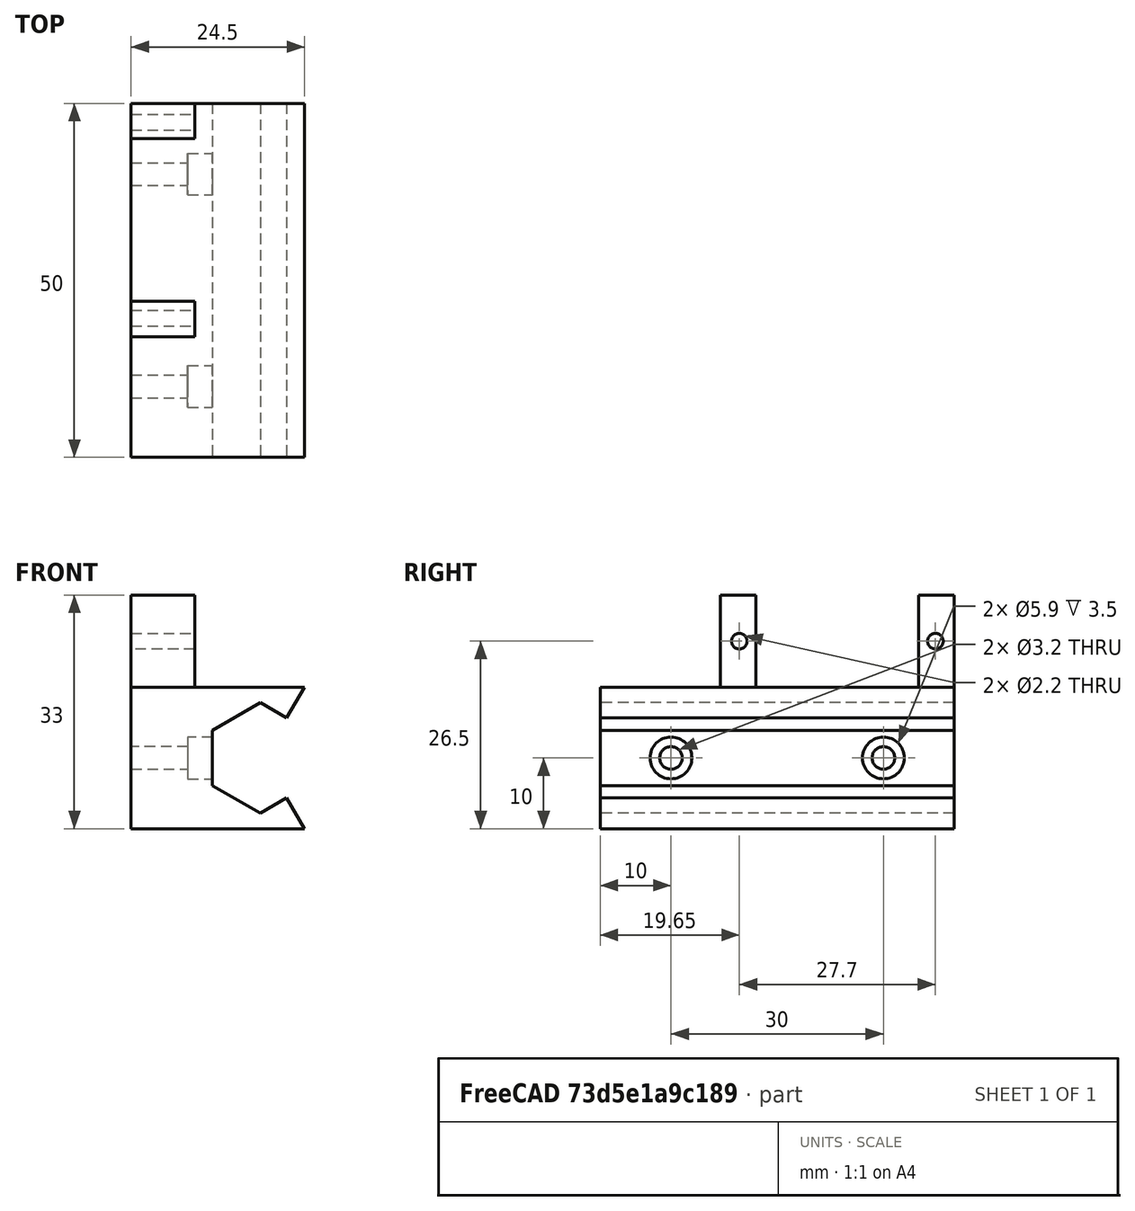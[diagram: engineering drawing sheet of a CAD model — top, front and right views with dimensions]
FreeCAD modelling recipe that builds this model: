
FCSTD DOCUMENT  (FreeCAD 1.0R39109 (Git))
Label: buzzMeIN
License: All rights reserved
LicenseURL: https://en.wikipedia.org/wiki/All_rights_reserved
objects: Sketcher::SketchObject×3, PartDesign::Body×2, PartDesign::Pad×2, PartDesign::SubShapeBinder×2, PartDesign::Pocket×2, Mesh::Feature×1
note: 22 computed .brp shape members not serialized (recipe doc carries the construction recipe); baked Part::Feature solids carry a one-line shape summary decoded from their .brp

FEATURE [PartDesign::Body] Body  label="Körper"
  AllowCompound = false
  Origin = -> Origin
FEATURE [Mesh::Feature] buzzMeIn_Penmover  label="buzzMeIn-Penmover"
FEATURE [Sketcher::SketchObject] Sketch
  ArcFitTolerance = 1e-06
  AttachmentSupport = -> [XZ_Plane001]
  FullyConstrained = true
  MakeInternals = false
  MapMode = 5
  Placement = pos=(0,0,0) rot=(1,0,0;1.5708rad)
  sketch-geometry (15):
    g0: LineSegment StartX=0 StartY=7.8 StartZ=0 EndX=-6.755 EndY=3.9 EndZ=0
    g1: LineSegment StartX=-6.755 StartY=3.9 StartZ=0 EndX=-6.755 EndY=-3.9 EndZ=0
    g2: LineSegment StartX=-6.755 StartY=-3.9 StartZ=0 EndX=0 EndY=-7.8 EndZ=0
    g3: Circle [constr] CenterX=0 CenterY=0 CenterZ=0 NormalX=0 NormalY=0 NormalZ=1 AngleXU=0 Radius=7.8
    g4: LineSegment StartX=3.72391 StartY=5.65 StartZ=0 EndX=0 EndY=7.8 EndZ=0
    g5: LineSegment StartX=0 StartY=-7.8 StartZ=0 EndX=3.72391 EndY=-5.65 EndZ=0
    g6: LineSegment [constr] StartX=3.72391 StartY=5.65 StartZ=0 EndX=3.72391 EndY=-5.65 EndZ=0
    g7: LineSegment [constr] StartX=3.72391 StartY=-5.65 StartZ=0 EndX=6.755 EndY=-3.9 EndZ=0
    g8: LineSegment [constr] StartX=3.72391 StartY=5.65 StartZ=0 EndX=6.755 EndY=3.9 EndZ=0
    g9: LineSegment [constr] StartX=6.755 StartY=3.9 StartZ=0 EndX=6.755 EndY=-3.9 EndZ=0
    g10: LineSegment StartX=3.72391 StartY=-5.65 StartZ=0 EndX=6.23538 EndY=-10 EndZ=0
    g11: LineSegment StartX=6.23538 StartY=-10 StartZ=0 EndX=-9.26 EndY=-10 EndZ=0
    g12: LineSegment StartX=-9.26 StartY=-10 StartZ=0 EndX=-9.26 EndY=10 EndZ=0
    g13: LineSegment StartX=-9.26 StartY=10 StartZ=0 EndX=6.23538 EndY=10 EndZ=0
    g14: LineSegment StartX=3.72391 StartY=5.65 StartZ=0 EndX=6.23538 EndY=10 EndZ=0
  constraints (41):
    c: Coincident(g0,g1)
    c: Coincident(g1,g2)
    c: Coincident(g2,g5)
    c: Coincident(g4,g0)
    c: Equal(g0,g1)
    c: Equal(g0,g2)
    c: PointOnObject(g0,g3)
    c: PointOnObject(g1,g3)
    c: PointOnObject(g2,g3)
    c: PointOnObject(g4,g3)
    c: Coincident(g3,g-1)
    c: PointOnObject(g0,g-2)
    c: Diameter(g3) = 15.6
    c: Vertical(g6)
    c: PointOnObject(g7,g3)
    c: PointOnObject(g8,g3)
    c: Parallel(g8,g4)
    c: Parallel(g7,g5)
    c: Coincident(g9,g8)
    c: Coincident(g9,g7)
    c: Vertical(g9)
    c: Equal(g9,g0)
    c: PointOnObject(g2,g-2)
    c: Horizontal(g11)
    c: Coincident(g12,g11)
    c: Vertical(g12)
    c: Coincident(g13,g12)
    c: Horizontal(g13)
    c: DistanceY(g12,g12) = 20
    c: Distance(g12,g-2) = 9.26
    c: Symmetric(g10,g13,g-1)
    c: Coincident(g5,g10)
    c: Coincident(g5,g7)
    c: Coincident(g4,g14)
    c: Coincident(g4,g8)
    c: Coincident(g6,g4)
    c: Coincident(g14,g13)
    c: Coincident(g6,g5)
    c: Coincident(g10,g11)
    c: Distance(g5,g5) = 4.3
    c: Angle(g10,g11) = 1.0472
FEATURE [PartDesign::Pad] Pad
  Direction = (0,-1,2e-16)
  Length = 50
  Length2 = 10
  Placement = pos=(0,0,0) rot=(1,0,0;1.5708rad)
  Profile = -> Sketch
  ReferenceAxis = -> Sketch [N_Axis]
  Refine = true
  Suppressed = false
  Type = 0
FEATURE [Sketcher::SketchObject] Sketch001
  ArcFitTolerance = 1e-06
  AttachmentSupport = -> [Pad]
  ExternalGeometry = -> [Pad]
  FullyConstrained = true
  MakeInternals = false
  MapMode = 5
  Placement = pos=(-9.26,0,0) rot=(0.707107,0,-0.707107;3.14159rad)
  sketch-geometry (15):
    g0: LineSegment StartX=-10 StartY=-2.7e-15 StartZ=0 EndX=10 EndY=-2.7e-15 EndZ=0
    g1: LineSegment StartX=10 StartY=-2.7e-15 StartZ=0 EndX=10 EndY=50 EndZ=0
    g2: LineSegment StartX=-10 StartY=5 StartZ=0 EndX=-23 EndY=5 EndZ=0
    g3: LineSegment StartX=-23 StartY=5 StartZ=0 EndX=-23 EndY=-2.7e-15 EndZ=0
    g4: LineSegment StartX=-23 StartY=-2.7e-15 StartZ=0 EndX=-10 EndY=-2.7e-15 EndZ=0
    g5: LineSegment StartX=-10 StartY=33 StartZ=0 EndX=-23 EndY=33 EndZ=0
    g6: LineSegment StartX=-23 StartY=33 StartZ=0 EndX=-23 EndY=28 EndZ=0
    g7: LineSegment StartX=-23 StartY=28 StartZ=0 EndX=-10 EndY=28 EndZ=0
    g8: LineSegment StartX=-10 StartY=5 StartZ=0 EndX=-10 EndY=28 EndZ=0
    g9: Circle CenterX=-16.5 CenterY=30.35 CenterZ=0 NormalX=0 NormalY=0 NormalZ=1 AngleXU=0 Radius=1.1
    g10: Circle CenterX=-16.5 CenterY=2.65 CenterZ=0 NormalX=0 NormalY=0 NormalZ=1 AngleXU=0 Radius=1.1
    g11: LineSegment [constr] StartX=-16.5 StartY=30.35 StartZ=0 EndX=-16.5 EndY=2.65 EndZ=0
    g12: LineSegment [constr] StartX=-10 StartY=16.5 StartZ=0 EndX=-23 EndY=16.5 EndZ=0
    g13: LineSegment StartX=10 StartY=50 StartZ=0 EndX=-10 EndY=50 EndZ=0
    g14: LineSegment StartX=-10 StartY=50 StartZ=0 EndX=-10 EndY=33 EndZ=0
  constraints (38):
    c: Coincident(g0,g1)
    c: Coincident(g2,g3)
    c: Coincident(g3,g4)
    c: Vertical(g3)
    c: Horizontal(g2)
    c: Horizontal(g4)
    c: Coincident(g5,g6)
    c: Coincident(g6,g7)
    c: Horizontal(g5)
    c: Horizontal(g7)
    c: Vertical(g6)
    c: Coincident(g8,g7)
    c: Vertical(g8)
    c: DistanceY(g6,g6) = 5
    c: DistanceY(g3,g3) = 5
    c: Vertical(g2,g6)
    c: DistanceY(g8,g8) = 23
    c: Coincident(g0,g-3)
    c: DistanceX(g5,g5) = 13
    c: Coincident(g0,g-4)
    c: Equal(g10,g9)
    c: Diameter(g9) = 2.2
    c: DistanceY(g10,g9) = 27.7
    c: Coincident(g11,g9)
    c: Coincident(g11,g10)
    c: Symmetric(g2,g2,g11)
    c: Coincident(g2,g8)
    c: PointOnObject(g2,g-3)
    c: Coincident(g4,g0)
    c: PointOnObject(g5,g-3)
    c: Symmetric(g8,g8,g12)
    c: Vertical(g6,g12)
    c: Symmetric(g9,g10,g12)
    c: Coincident(g1,g-4)
    c: Coincident(g13,g1)
    c: Coincident(g13,g-3)
    c: Coincident(g14,g13)
    c: Coincident(g14,g5)
FEATURE [PartDesign::Pad] Pad001
  BaseFeature = -> Pad
  Direction = (-1,0,-2e-16)
  Length = 9
  Length2 = 10
  Placement = pos=(0,0,0) rot=(1,0,0;1.5708rad)
  Profile = -> Sketch001
  ReferenceAxis = -> Sketch001 [N_Axis]
  Refine = true
  Suppressed = false
  Type = 0
FEATURE [Sketcher::SketchObject] Sketch002
  ArcFitTolerance = 1e-06
  AttachmentSupport = -> [Pad001]
  ExternalGeometry = -> [Pad001]
  FullyConstrained = true
  MakeInternals = false
  MapMode = 5
  Placement = pos=(-6.755,0,2.2083e-12) rot=(0.707107,0,0.707107;3.14159rad)
  sketch-geometry (5):
    g0: Circle CenterX=0 CenterY=40 CenterZ=0 NormalX=0 NormalY=0 NormalZ=1 AngleXU=0 Radius=2.95
    g1: Circle CenterX=-6.4e-15 CenterY=10 CenterZ=0 NormalX=0 NormalY=0 NormalZ=1 AngleXU=0 Radius=2.95
    g2: LineSegment [constr] StartX=-10 StartY=25 StartZ=0 EndX=0 EndY=25 EndZ=0
    g3: Circle CenterX=0 CenterY=40 CenterZ=0 NormalX=0 NormalY=0 NormalZ=1 AngleXU=0 Radius=1.6
    g4: Circle CenterX=-6.4e-15 CenterY=10 CenterZ=0 NormalX=0 NormalY=0 NormalZ=1 AngleXU=0 Radius=1.6
  constraints (12):
    c: PointOnObject(g0,g-2)
    c: Diameter(g0) = 5.9
    c: Equal(g0,g1)
    c: Symmetric(g-3,g-3,g2)
    c: PointOnObject(g2,g-3)
    c: Symmetric(g1,g0,g2)
    c: DistanceY(g1,g0) = 30
    c: PointOnObject(g2,g-2)
    c: Coincident(g3,g0)
    c: Coincident(g4,g1)
    c: Diameter(g3) = 3.2
    c: Equal(g4,g3)
FEATURE [PartDesign::SubShapeBinder] Binder
  BindCopyOnChange = 0
  BindMode = 0
  ClaimChildren = false
  Context = -> Body001 [Binder.]
  Fuse = false
  MakeFace = true
  OffsetFill = false
  OffsetIntersection = false
  OffsetJoinType = 0
  OffsetOpenResult = false
  PartialLoad = false
  Refine = true
  Relative = true
  Support = -> [Sketch002[Edge1,Edge2]]
  _Version = 2
FEATURE [PartDesign::SubShapeBinder] Binder001
  BindCopyOnChange = 0
  BindMode = 0
  ClaimChildren = false
  Context = -> Body001 [Binder001.]
  Fuse = false
  MakeFace = true
  OffsetFill = false
  OffsetIntersection = false
  OffsetJoinType = 0
  OffsetOpenResult = false
  PartialLoad = false
  Refine = true
  Relative = true
  Support = -> [Sketch002[Edge3,Edge4]]
  _Version = 2
FEATURE [PartDesign::Pocket] Pocket
  BaseFeature = -> Pad001
  Direction = (-1,0,3.268e-13)
  Length = 3.5
  Length2 = 5
  Placement = pos=(0,0,0) rot=(1,0,0;1.5708rad)
  Profile = -> Binder
  Refine = true
  Suppressed = false
  Type = 0
FEATURE [PartDesign::Pocket] Pocket001
  BaseFeature = -> Pocket
  Direction = (-1,0,3.268e-13)
  Length = 5
  Length2 = 5
  Placement = pos=(0,0,0) rot=(1,0,0;1.5708rad)
  Profile = -> Binder001
  Refine = true
  Suppressed = false
  Type = 1
FEATURE [PartDesign::Body] Body001  label="Körper001"
  AllowCompound = false
  Group = -> [Sketch,Pad,Sketch001,Pad001,Sketch002,Binder,Binder001,Pocket,Pocket001]
  Origin = -> Origin001
  Tip = -> Pocket001
